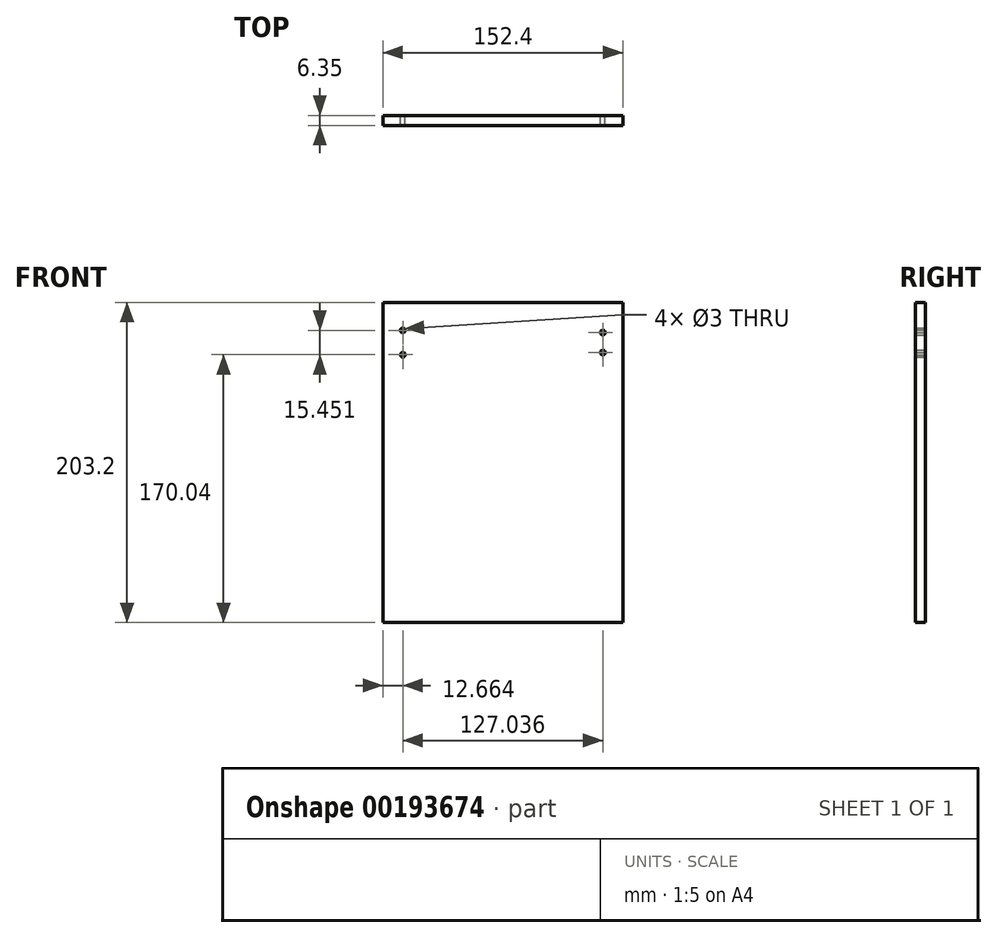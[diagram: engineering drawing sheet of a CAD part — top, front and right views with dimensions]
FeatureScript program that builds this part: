
annotation { "Feature Type Name" : "Feature", "Feature Type Description" : "" }
export const myFeature = defineFeature(function(context is Context, id is Id, definition is map)
    precondition{}
    {
        {
            var Q0;
            Q0=qCreatedBy(makeId("Front.planeOp"),FACE);
            var sketch = newSketch(context, id + "F0", { "sketchPlane" : qUnion([Q0])});
            skLineSegment(sketch, "E0.bottom", {"start": v(76.2, -101.6) * mm, "end": v(-76.2, -101.6) * mm});
            skLineSegment(sketch, "E0.top", {"start": v(76.2, 101.6) * mm, "end": v(-76.2, 101.6) * mm});
            skLineSegment(sketch, "E0.left", {"start": v(76.2, -101.6) * mm, "end": v(76.2, 101.6) * mm});
            skLineSegment(sketch, "E0.right", {"start": v(-76.2, -101.6) * mm, "end": v(-76.2, 101.6) * mm});
            skPoint(sketch, "E0.middle", {"position": v(0, 0) * mm});
            skSolve(sketch);
        }
        {
            var Q0;
            Q0=makeQuery(id+"F0.imprint","IMPRINT",FACE,{"disambiguationData":[TD([[makeQuery(id+"F0.imprint","IMPRINT",EDGE,{"derivedFrom":sQuery(id+"F0.wireOp",EDGE,"E0.bottom")}),-1.0]])]});
            extrude(context, id + "F1", {"entities" : qUnion([Q0]), "depth" : 6.35 * mm});
        }
        {
            var Q0;
            Q0=qCreatedBy(makeId("Front.planeOp"),FACE);
            var sketch = newSketch(context, id + "F2", { "sketchPlane" : qUnion([Q0])});
            skCircle(sketch, "E1", {"center": v(-63.54, 83.9) * mm, "radius": 1.5 * mm});
            skCircle(sketch, "E2", {"center": v(-63.47, 68.44) * mm, "radius": 1.5 * mm});
            skSolve(sketch);
        }
        {
            var Q0;
            Q0=qCreatedBy(makeId("Front.planeOp"),FACE);
            var sketch = newSketch(context, id + "F3", { "sketchPlane" : qUnion([Q0])});
            skLineSegment(sketch, "E3", {"start": v(63.5, 101.56) * mm, "end": v(63.5, 82.5) * mm});
            skLineSegment(sketch, "E4", {"start": v(63.5, 82.5) * mm, "end": v(63.5, 69.8) * mm});
            skCircle(sketch, "E5", {"center": v(63.5, 82.5) * mm, "radius": 1.5 * mm});
            skCircle(sketch, "E6", {"center": v(63.5, 69.8) * mm, "radius": 1.5 * mm});
            skSolve(sketch);
        }
        {
            var Q0;
            Q0=makeQuery(id+"F2.imprint","IMPRINT",FACE,{"disambiguationData":[TD([[makeQuery(id+"F2.imprint","IMPRINT",EDGE,{"derivedFrom":sQuery(id+"F2.wireOp",EDGE,"E1")}),1.0]])]});
            var Q1;
            Q1=makeQuery(id+"F2.imprint","IMPRINT",FACE,{"disambiguationData":[TD([[makeQuery(id+"F2.imprint","IMPRINT",EDGE,{"derivedFrom":sQuery(id+"F2.wireOp",EDGE,"E2")}),1.0]])]});
            extrude(context, id + "F4", {"entities" : qUnion([Q0, Q1]), "operationType" : NewBodyOperationType.REMOVE, "depth" : 14.4 * mm});
        }
        {
            var Q0;
            {var subQ0=sQuery(id+"F3.wireOp",EDGE,"E4");var subQ1=sQuery(id+"F3.wireOp",EDGE,"E3");var subQ2=makeQuery(id+"F3.imprint","INTERSECT",VERTEX,{"derivedFrom":[subQ1,subQ0]});Q0=makeQuery(id+"F3.imprint","IMPRINT",FACE,{"disambiguationData":[TD([[makeQuery(id+"F3.imprint","IMPRINT",EDGE,{"disambiguationData":[TD([[subQ2,1.0]])],"derivedFrom":subQ1}),1.0]])]});}
            var Q1;
            Q1=makeQuery(id+"F3.imprint","IMPRINT",FACE,{"disambiguationData":[TD([[makeQuery(id+"F3.imprint","IMPRINT",EDGE,{"derivedFrom":sQuery(id+"F3.wireOp",EDGE,"E6")}),1.0]])]});
            var Q2;
            {var subQ0=sQuery(id+"F3.wireOp",EDGE,"E4");var subQ1=sQuery(id+"F3.wireOp",EDGE,"E3");var subQ2=makeQuery(id+"F3.imprint","INTERSECT",VERTEX,{"derivedFrom":[subQ1,subQ0]});Q2=makeQuery(id+"F3.imprint","IMPRINT",FACE,{"disambiguationData":[TD([[makeQuery(id+"F3.imprint","IMPRINT",EDGE,{"disambiguationData":[TD([[subQ2,1.0]])],"derivedFrom":subQ1}),-1.0]])]});}
            extrude(context, id + "F5", {"entities" : qUnion([Q0, Q1, Q2]), "operationType" : NewBodyOperationType.REMOVE, "depth" : 25.4 * mm});
        }
    });
